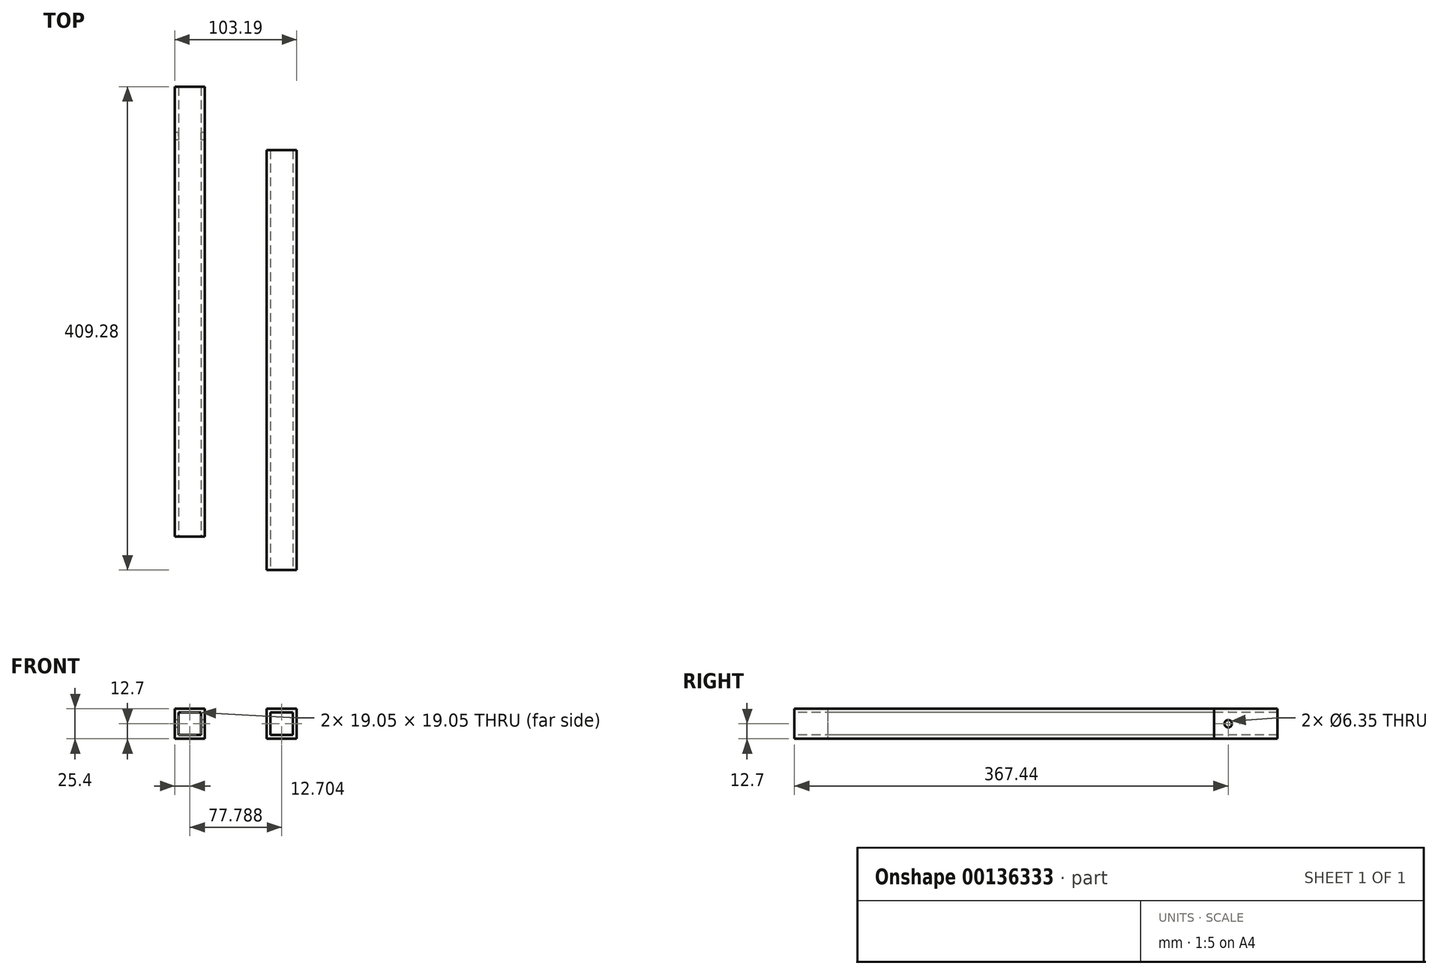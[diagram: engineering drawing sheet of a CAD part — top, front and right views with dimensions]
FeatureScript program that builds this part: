
annotation { "Feature Type Name" : "Feature", "Feature Type Description" : "" }
export const myFeature = defineFeature(function(context is Context, id is Id, definition is map)
    precondition{}
    {
        {
            var Q0;
            Q0=qCreatedBy(makeId("Top.planeOp"),FACE);
            var sketch = newSketch(context, id + "F0", { "sketchPlane" : qUnion([Q0])});
            skLineSegment(sketch, "E0.bottom", {"start": v(-47.29, 361.6) * mm, "end": v(-21.89, 361.6) * mm});
            skLineSegment(sketch, "E0.top", {"start": v(-47.29, -19.4) * mm, "end": v(-21.89, -19.4) * mm});
            skLineSegment(sketch, "E0.left", {"start": v(-47.29, 361.6) * mm, "end": v(-47.29, -19.4) * mm});
            skLineSegment(sketch, "E0.right", {"start": v(-21.89, 361.6) * mm, "end": v(-21.89, -19.4) * mm});
            skLineSegment(sketch, "E1.bottom", {"start": v(30.5, 307.92) * mm, "end": v(55.9, 307.92) * mm});
            skLineSegment(sketch, "E1.top", {"start": v(30.5, -47.68) * mm, "end": v(55.9, -47.68) * mm});
            skLineSegment(sketch, "E1.left", {"start": v(30.5, 307.92) * mm, "end": v(30.5, -47.68) * mm});
            skLineSegment(sketch, "E1.right", {"start": v(55.9, 307.92) * mm, "end": v(55.9, -47.68) * mm});
            skPoint(sketch, "E2", {"position": v(-34.59, 284.44) * mm});
            skPoint(sketch, "E2.positionSnap0", {"position": v(-34.59, 361.6) * mm});
            skPoint(sketch, "E3", {"position": v(-34.59, 78.78) * mm});
            skSolve(sketch);
        }
        {
            var Q0;
            Q0 = qSketchRegion(id + "F0", true);
            extrude(context, id + "F1", {"entities" : qUnion([Q0]), "depth" : 25.4 * mm});
        }
        {
            var Q0;
            Q0=makeQuery(id+"F1.opExtrude","SWEPT_FACE",FACE,{"disambiguationData":[OSD([sQuery(id+"F0.wireOp",EDGE,"E0.top")])]});
            var Q1;
            Q1=makeQuery(id+"F1.opExtrude","SWEPT_FACE",FACE,{"disambiguationData":[OSD([sQuery(id+"F0.wireOp",EDGE,"E1.top")])]});
            var Q2;
            Q2=makeQuery(id+"F1.opExtrude","SWEPT_FACE",FACE,{"disambiguationData":[OSD([sQuery(id+"F0.wireOp",EDGE,"E0.bottom")])]});
            var Q3;
            Q3=makeQuery(id+"F1.opExtrude","SWEPT_FACE",FACE,{"disambiguationData":[OSD([sQuery(id+"F0.wireOp",EDGE,"E1.bottom")])]});
            shell(context, id + "F2", {"entities" : qUnion([Q0, Q1, Q2, Q3]), "thickness" : 3.17 * mm});
        }
        {
            var Q0;
            Q0=makeQuery(id+"F1.opExtrude","SWEPT_FACE",FACE,{"disambiguationData":[OSD([sQuery(id+"F0.wireOp",EDGE,"E0.left")])]});
            var sketch = newSketch(context, id + "F3", { "sketchPlane" : qUnion([Q0])});
            skCircle(sketch, "E4", {"center": v(-319.76, 12.7) * mm, "radius": 10.46 * mm});
            skLineSegment(sketch, "E5", {"start": v(-361.6, 12.7) * mm, "end": v(-319.76, 12.7) * mm, "construction": true});
            skSolve(sketch);
        }
        {
            var Q0;
            Q0=sQuery(id+"F3.wireOp",VERTEX,"E5.end");
            var Q1;
            Q1=makeQuery(id+"F1.opExtrude","SWEPT_BODY",BODY,{"disambiguationData":[OSD([sQuery(id+"F0.wireOp",EDGE,"E0.bottom"),sQuery(id+"F0.wireOp",EDGE,"E0.top"),sQuery(id+"F0.wireOp",EDGE,"E0.left"),sQuery(id+"F0.wireOp",EDGE,"E0.right")])]});
            hole(context, id + "F4", {"style" : HoleStyle.SIMPLE, "endStyle" : HoleEndStyle.THROUGH, "holeDiameter" : 6.35 * mm, "locations" : qUnion([Q0]), "scope" : qUnion([Q1]), "isTappedThrough" : true});
        }
    });
